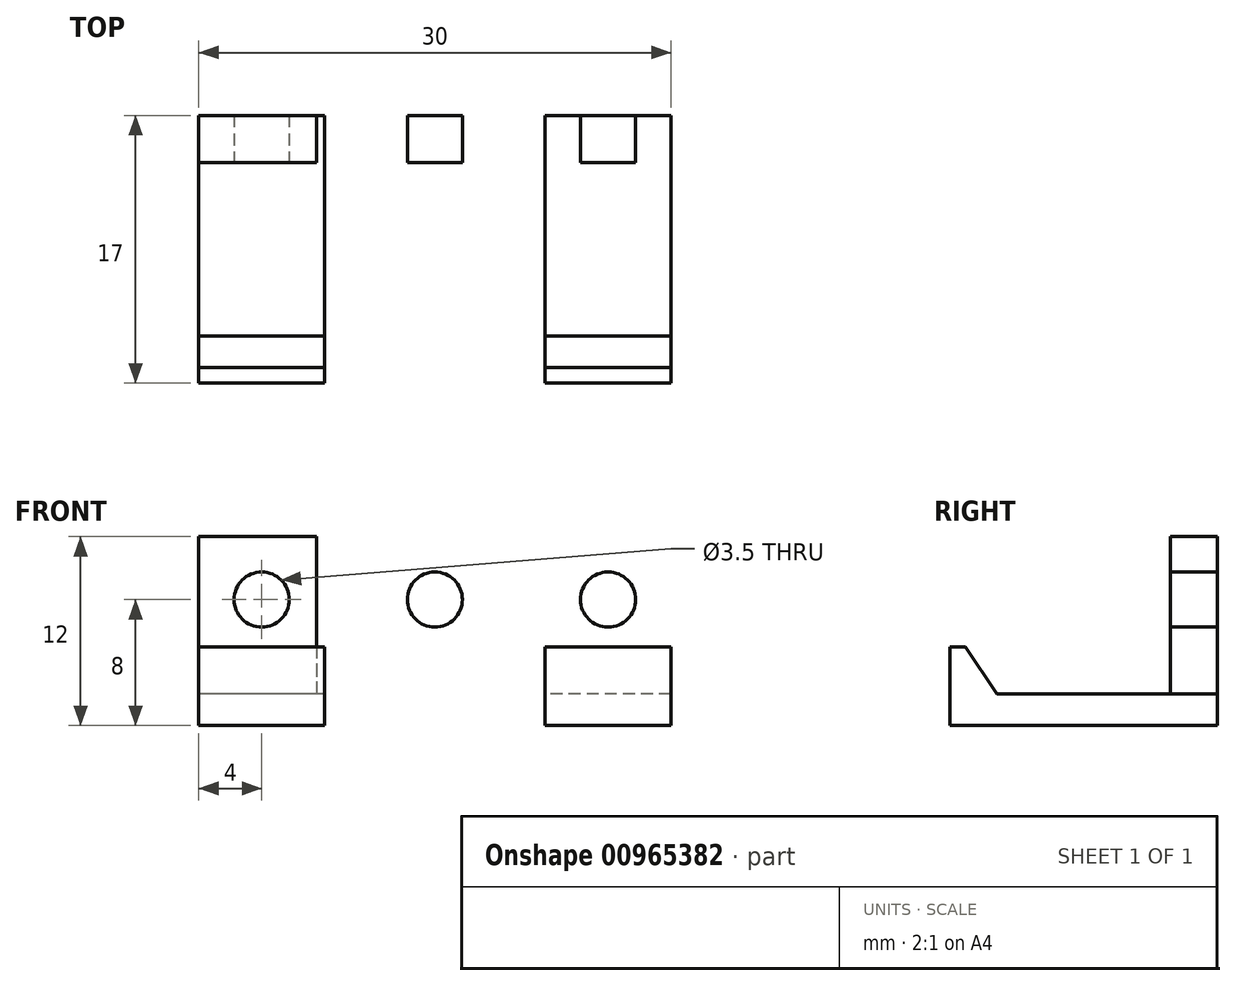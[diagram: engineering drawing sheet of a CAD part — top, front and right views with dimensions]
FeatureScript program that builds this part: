
annotation { "Feature Type Name" : "Feature", "Feature Type Description" : "" }
export const myFeature = defineFeature(function(context is Context, id is Id, definition is map)
    precondition{}
    {
        {
            var Q0;
            Q0=qCreatedBy(makeId("Top.planeOp"),FACE);
            var sketch = newSketch(context, id + "F0", { "sketchPlane" : qUnion([Q0])});
            skLineSegment(sketch, "E0.bottom", {"start": v(0, 0) * mm, "end": v(-30, 0) * mm});
            skLineSegment(sketch, "E0.top", {"start": v(0, 3) * mm, "end": v(-30, 3) * mm});
            skLineSegment(sketch, "E0.left", {"start": v(0, 0) * mm, "end": v(0, 3) * mm});
            skLineSegment(sketch, "E0.right", {"start": v(-30, 0) * mm, "end": v(-30, 3) * mm});
            skLineSegment(sketch, "E1.bottom", {"start": v(-30, 0) * mm, "end": v(-22, 0) * mm});
            skLineSegment(sketch, "E1.top", {"start": v(-30, -14) * mm, "end": v(-22, -14) * mm});
            skLineSegment(sketch, "E1.left", {"start": v(-30, 0) * mm, "end": v(-30, -14) * mm});
            skLineSegment(sketch, "E1.right", {"start": v(-22, 0) * mm, "end": v(-22, -14) * mm});
            skLineSegment(sketch, "E2", {"start": v(-15, 3) * mm, "end": v(-15, 0) * mm});
            skLineSegment(sketch, "E3.MirrorCS", {"start": v(-8, 0) * mm, "end": v(-8, -14) * mm});
            skLineSegment(sketch, "E4.MirrorCS", {"start": v(0, -14) * mm, "end": v(-8, -14) * mm});
            skLineSegment(sketch, "E5.MirrorCS", {"start": v(0, 0) * mm, "end": v(0, -14) * mm});
            skSolve(sketch);
        }
        {
            var Q0;
            Q0=makeQuery(id+"F0.imprint","IMPRINT",FACE,{"disambiguationData":[TD([[makeQuery(id+"F0.imprint","IMPRINT",EDGE,{"derivedFrom":sQuery(id+"F0.wireOp",EDGE,"E1.top")}),1.0]])]});
            var Q1;
            {var subQ2=sQuery(id+"F0.wireOp",EDGE,"E0.right");Q1=makeQuery(id+"F0.imprint","IMPRINT",FACE,{"disambiguationData":[TD([[makeQuery(id+"F0.imprint","IMPRINT",EDGE,{"derivedFrom":subQ2}),-1.0]])]});}
            var Q2;
            {var subQ0=sQuery(id+"F0.wireOp",EDGE,"E0.left");Q2=makeQuery(id+"F0.imprint","IMPRINT",FACE,{"disambiguationData":[TD([[makeQuery(id+"F0.imprint","IMPRINT",EDGE,{"derivedFrom":subQ0}),1.0]])]});}
            var Q3;
            {var subQ2=sQuery(id+"F0.wireOp",EDGE,"E3.MirrorCS");Q3=makeQuery(id+"F0.imprint","IMPRINT",FACE,{"disambiguationData":[TD([[makeQuery(id+"F0.imprint","IMPRINT",EDGE,{"derivedFrom":subQ2}),1.0]])]});}
            extrude(context, id + "F1", {"entities" : qUnion([Q0, Q1, Q2, Q3]), "depth" : 2 * mm, "offsetDistance" : 25 * mm});
        }
        {
            var Q0;
            Q0=makeQuery(id+"F1.opExtrude","CAP_FACE",FACE,{"disambiguationData":[OSD([sQuery(id+"F0.wireOp",EDGE,"E0.bottom"),sQuery(id+"F0.wireOp",EDGE,"E0.top"),sQuery(id+"F0.wireOp",EDGE,"E0.left"),sQuery(id+"F0.wireOp",EDGE,"E0.right"),sQuery(id+"F0.wireOp",EDGE,"E1.top"),sQuery(id+"F0.wireOp",EDGE,"E1.left"),sQuery(id+"F0.wireOp",EDGE,"E1.right"),sQuery(id+"F0.wireOp",EDGE,"E3.MirrorCS"),sQuery(id+"F0.wireOp",EDGE,"E4.MirrorCS"),sQuery(id+"F0.wireOp",EDGE,"E5.MirrorCS")])],"isStart":false});
            var sketch = newSketch(context, id + "F2", { "sketchPlane" : qUnion([Q0])});
            skLineSegment(sketch, "E6.bottom", {"start": v(-30, 3) * mm, "end": v(0, 3) * mm});
            skLineSegment(sketch, "E6.top", {"start": v(-30, 0) * mm, "end": v(0, 0) * mm});
            skLineSegment(sketch, "E6.left", {"start": v(-30, 3) * mm, "end": v(-30, 0) * mm});
            skLineSegment(sketch, "E6.right", {"start": v(0, 3) * mm, "end": v(0, 0) * mm});
            skSolve(sketch);
        }
        {
            var Q0;
            Q0=makeQuery(id+"F2.imprint","IMPRINT",FACE,{"disambiguationData":[TD([[makeQuery(id+"F2.imprint","IMPRINT",EDGE,{"derivedFrom":sQuery(id+"F2.wireOp",EDGE,"E6.bottom")}),1.0]])]});
            extrude(context, id + "F3", {"entities" : qUnion([Q0]), "operationType" : NewBodyOperationType.ADD, "depth" : 10 * mm, "offsetDistance" : 25 * mm});
        }
        {
            var Q0;
            Q0=makeQuery(id+"F3.boolean.opBoolean","MERGE",FACE,{"derivedFrom":[makeQuery(id+"F1.opExtrude","SWEPT_FACE",FACE,{"disambiguationData":[OSD([sQuery(id+"F0.wireOp",EDGE,"E0.bottom")])]}),makeQuery(id+"F3.opExtrude","SWEPT_FACE",FACE,{"disambiguationData":[OSD([sQuery(id+"F2.wireOp",EDGE,"E6.top")])]})]});
            var sketch = newSketch(context, id + "F4", { "sketchPlane" : qUnion([Q0])});
            skLineSegment(sketch, "E7", {"start": v(-15, 12) * mm, "end": v(-15, 0) * mm});
            skLineSegment(sketch, "E8", {"start": v(-15, 12) * mm, "end": v(-30, 12) * mm});
            skLineSegment(sketch, "E9", {"start": v(-22.5, 12) * mm, "end": v(-22.5, 0) * mm});
            skCircle(sketch, "E10", {"center": v(-26, 8) * mm, "radius": 1.75 * mm});
            skCircle(sketch, "E11.MirrorC", {"center": v(-4, 8) * mm, "radius": 1.75 * mm});
            skCircle(sketch, "E12", {"center": v(-15, 8) * mm, "radius": 1.75 * mm});
            skSolve(sketch);
        }
        {
            var Q0;
            Q0=makeQuery(id+"F4.imprint","IMPRINT",FACE,{"disambiguationData":[TD([[makeQuery(id+"F4.imprint","IMPRINT",EDGE,{"derivedFrom":sQuery(id+"F4.wireOp",EDGE,"E10")}),1.0]])]});
            var Q1;
            {var subQ0=sQuery(id+"F4.wireOp",EDGE,"E12");var subQ1=sQuery(id+"F4.wireOp",EDGE,"E7");var subQ2=makeQuery(id+"F4.imprint","INTERSECT",VERTEX,{"disambiguationData":[OD(0.0)],"derivedFrom":[subQ1,subQ0]});Q1=makeQuery(id+"F4.imprint","IMPRINT",FACE,{"disambiguationData":[TD([[makeQuery(id+"F4.imprint","IMPRINT",EDGE,{"disambiguationData":[TD([[subQ2,-1.0]])],"derivedFrom":subQ1}),-1.0]])]});}
            var Q2;
            {var subQ0=sQuery(id+"F4.wireOp",EDGE,"E12");var subQ1=sQuery(id+"F4.wireOp",EDGE,"E7");var subQ2=makeQuery(id+"F4.imprint","INTERSECT",VERTEX,{"disambiguationData":[OD(0.0)],"derivedFrom":[subQ1,subQ0]});Q2=makeQuery(id+"F4.imprint","IMPRINT",FACE,{"disambiguationData":[TD([[makeQuery(id+"F4.imprint","IMPRINT",EDGE,{"disambiguationData":[TD([[subQ2,-1.0]])],"derivedFrom":subQ1}),1.0]])]});}
            var Q3;
            Q3=makeQuery(id+"F4.imprint","IMPRINT",FACE,{"disambiguationData":[TD([[makeQuery(id+"F4.imprint","IMPRINT",EDGE,{"derivedFrom":sQuery(id+"F4.wireOp",EDGE,"E11.MirrorC")}),-1.0]])]});
            extrude(context, id + "F5", {"entities" : qUnion([Q0, Q1, Q2, Q3]), "operationType" : NewBodyOperationType.REMOVE, "oppositeDirection" : true, "depth" : 25 * mm, "offsetDistance" : 25 * mm});
        }
        {
            var Q0;
            Q0=makeQuery(id+"F3.boolean.opBoolean","MERGE",FACE,{"derivedFrom":[makeQuery(id+"F1.opExtrude","SWEPT_FACE",FACE,{"disambiguationData":[OSD([sQuery(id+"F0.wireOp",EDGE,"E0.right"),sQuery(id+"F0.wireOp",EDGE,"E1.left")])]}),makeQuery(id+"F3.opExtrude","SWEPT_FACE",FACE,{"disambiguationData":[OSD([sQuery(id+"F2.wireOp",EDGE,"E6.left")])]})]});
            var sketch = newSketch(context, id + "F6", { "sketchPlane" : qUnion([Q0])});
            skLineSegment(sketch, "E13", {"start": v(14, 2) * mm, "end": v(14, 5) * mm});
            skLineSegment(sketch, "E14", {"start": v(11, 2) * mm, "end": v(14, 2) * mm});
            skLineSegment(sketch, "E15", {"start": v(14, 5) * mm, "end": v(13, 5) * mm});
            skLineSegment(sketch, "E16", {"start": v(13, 5) * mm, "end": v(11, 2) * mm});
            skSolve(sketch);
        }
        {
            var Q0;
            Q0=makeQuery(id+"F6.imprint","IMPRINT",FACE,{"disambiguationData":[TD([[makeQuery(id+"F6.imprint","IMPRINT",EDGE,{"derivedFrom":sQuery(id+"F6.wireOp",EDGE,"E13")}),1.0]])]});
            extrude(context, id + "F7", {"entities" : qUnion([Q0]), "operationType" : NewBodyOperationType.ADD, "oppositeDirection" : true, "depth" : 30 * mm, "offsetDistance" : 25 * mm});
        }
        {
            var Q0;
            Q0=makeQuery(id+"F7.opExtrude","SWEPT_FACE",FACE,{"disambiguationData":[OSD([sQuery(id+"F6.wireOp",EDGE,"E14")])]});
            var sketch = newSketch(context, id + "F8", { "sketchPlane" : qUnion([Q0])});
            skLineSegment(sketch, "E17.bottom", {"start": v(-22, 14) * mm, "end": v(-8, 14) * mm});
            skLineSegment(sketch, "E17.top", {"start": v(-22, 11) * mm, "end": v(-8, 11) * mm});
            skLineSegment(sketch, "E17.left", {"start": v(-22, 14) * mm, "end": v(-22, 11) * mm});
            skLineSegment(sketch, "E17.right", {"start": v(-8, 14) * mm, "end": v(-8, 11) * mm});
            skSolve(sketch);
        }
        {
            var Q0;
            Q0=makeQuery(id+"F8.imprint","IMPRINT",FACE,{"disambiguationData":[TD([[makeQuery(id+"F8.imprint","IMPRINT",EDGE,{"derivedFrom":sQuery(id+"F8.wireOp",EDGE,"E17.bottom")}),1.0]])]});
            extrude(context, id + "F9", {"entities" : qUnion([Q0]), "operationType" : NewBodyOperationType.REMOVE, "oppositeDirection" : true, "depth" : 25 * mm, "offsetDistance" : 25 * mm});
        }
    });
